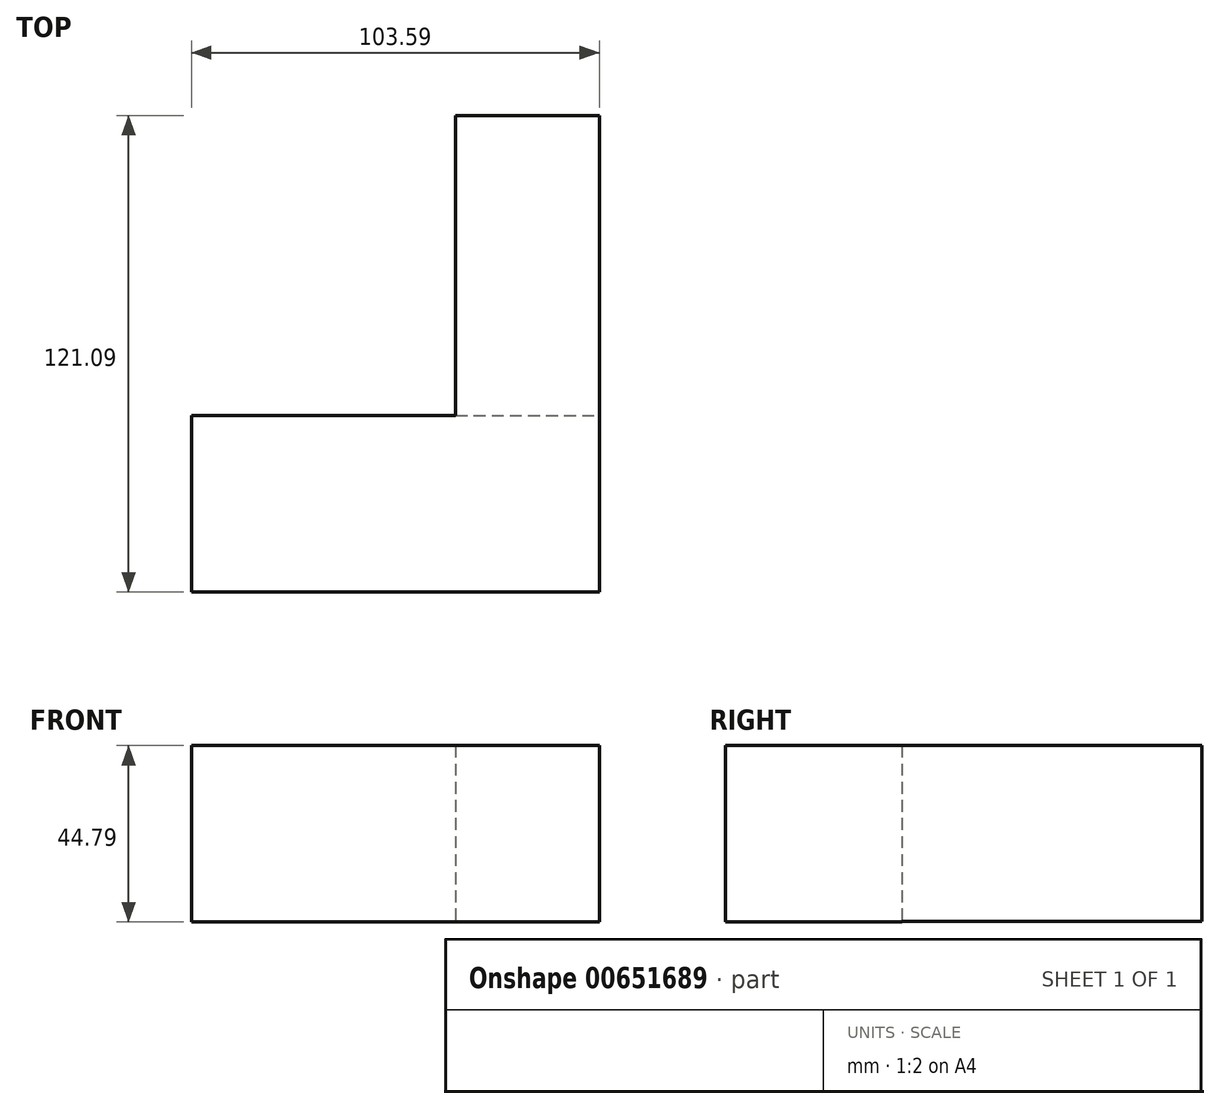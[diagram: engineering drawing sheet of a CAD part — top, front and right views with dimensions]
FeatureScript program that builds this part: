
annotation { "Feature Type Name" : "Feature", "Feature Type Description" : "" }
export const myFeature = defineFeature(function(context is Context, id is Id, definition is map)
    precondition{}
    {
        {
            var Q0;
            Q0=qCreatedBy(makeId("Front.planeOp"),FACE);
            var sketch = newSketch(context, id + "F0", { "sketchPlane" : qUnion([Q0])});
            skLineSegment(sketch, "E0.bottom", {"start": v(-36.51, 0) * mm, "end": v(0, 0) * mm});
            skLineSegment(sketch, "E0.top", {"start": v(-36.51, -44.66) * mm, "end": v(0, -44.66) * mm});
            skLineSegment(sketch, "E0.left", {"start": v(-36.51, 0) * mm, "end": v(-36.51, -44.66) * mm});
            skLineSegment(sketch, "E0.right", {"start": v(0, 0) * mm, "end": v(0, -44.66) * mm});
            skSolve(sketch);
        }
        {
            var Q0;
            Q0=makeQuery(id+"F0.imprint","IMPRINT",FACE,{"disambiguationData":[TD([[makeQuery(id+"F0.imprint","IMPRINT",EDGE,{"derivedFrom":sQuery(id+"F0.wireOp",EDGE,"E0.bottom")}),-1.0]])]});
            extrude(context, id + "F1", {"entities" : qUnion([Q0]), "oppositeDirection" : true, "depth" : 76.2 * mm, "offsetDistance" : 25.4 * mm});
        }
        {
            var Q0;
            Q0=qCreatedBy(makeId("Right.planeOp"),FACE);
            var sketch = newSketch(context, id + "F2", { "sketchPlane" : qUnion([Q0])});
            skLineSegment(sketch, "E1.bottom", {"start": v(-44.89, 0) * mm, "end": v(0, 0) * mm});
            skLineSegment(sketch, "E1.top", {"start": v(-44.89, -44.8) * mm, "end": v(0, -44.8) * mm});
            skLineSegment(sketch, "E1.left", {"start": v(-44.89, 0) * mm, "end": v(-44.89, -44.8) * mm});
            skLineSegment(sketch, "E1.right", {"start": v(0, 0) * mm, "end": v(0, -44.8) * mm});
            skSolve(sketch);
        }
        {
            var Q0;
            Q0=makeQuery(id+"F2.imprint","IMPRINT",FACE,{"disambiguationData":[TD([[makeQuery(id+"F2.imprint","IMPRINT",EDGE,{"derivedFrom":sQuery(id+"F2.wireOp",EDGE,"E1.bottom")}),-1.0]])]});
            extrude(context, id + "F3", {"entities" : qUnion([Q0]), "operationType" : NewBodyOperationType.ADD, "oppositeDirection" : true, "depth" : 103.6 * mm, "offsetDistance" : 25.4 * mm});
        }
    });
